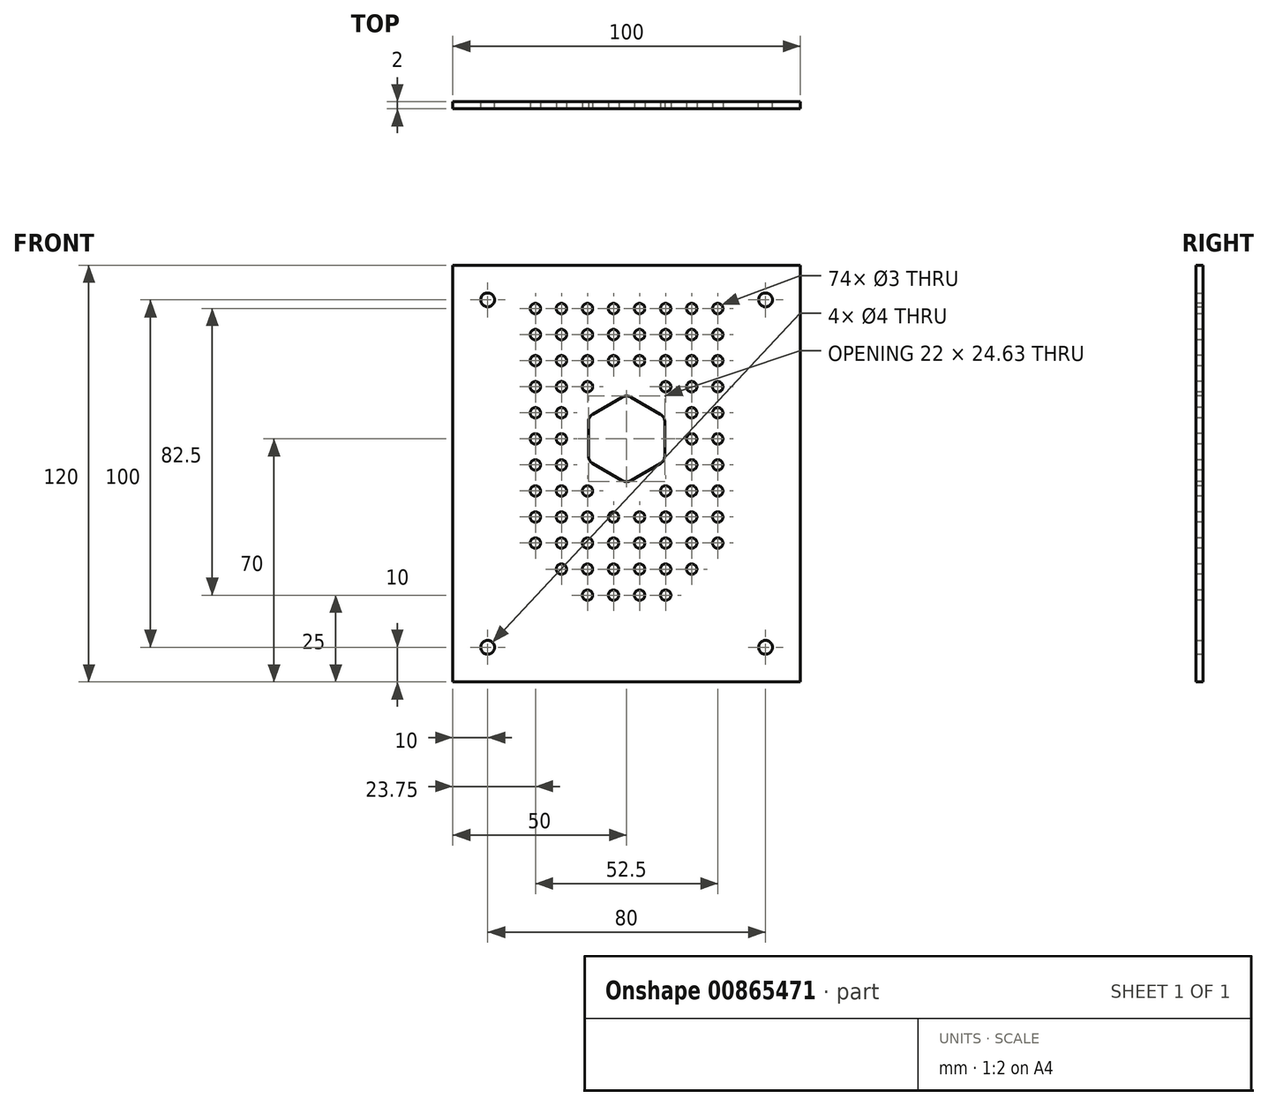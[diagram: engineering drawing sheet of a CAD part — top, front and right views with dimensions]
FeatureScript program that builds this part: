
annotation { "Feature Type Name" : "Feature", "Feature Type Description" : "" }
export const myFeature = defineFeature(function(context is Context, id is Id, definition is map)
    precondition{}
    {
        {
            var Q0;
            Q0=qCreatedBy(makeId("Front.planeOp"),FACE);
            var sketch = newSketch(context, id + "F0", { "sketchPlane" : qUnion([Q0])});
            skLineSegment(sketch, "E0.bottom", {"start": v(50, 60) * mm, "end": v(-50, 60) * mm});
            skLineSegment(sketch, "E0.top", {"start": v(50, -60) * mm, "end": v(-50, -60) * mm});
            skLineSegment(sketch, "E0.left", {"start": v(50, 60) * mm, "end": v(50, -60) * mm});
            skLineSegment(sketch, "E0.right", {"start": v(-50, 60) * mm, "end": v(-50, -60) * mm});
            skPoint(sketch, "E0.middle", {"position": v(0, 0) * mm});
            skCircle(sketch, "E1", {"center": v(-40, 50) * mm, "radius": 2 * mm});
            skCircle(sketch, "E2", {"center": v(40, 50) * mm, "radius": 2 * mm});
            skCircle(sketch, "E3", {"center": v(40, -50) * mm, "radius": 2 * mm});
            skCircle(sketch, "E4", {"center": v(-40, -50) * mm, "radius": 2 * mm});
            skSolve(sketch);
        }
        {
            var Q0;
            Q0 = qSketchRegion(id + "F0", true);
            extrude(context, id + "F1", {"entities" : qUnion([Q0]), "depth" : 2 * mm, "offsetDistance" : 25 * mm});
        }
        {
            var Q0;
            Q0=makeQuery(id+"F1.opExtrude","CAP_FACE",FACE,{"disambiguationData":[OSD([sQuery(id+"F0.wireOp",EDGE,"E0.bottom"),sQuery(id+"F0.wireOp",EDGE,"E0.top"),sQuery(id+"F0.wireOp",EDGE,"E0.left"),sQuery(id+"F0.wireOp",EDGE,"E0.right"),sQuery(id+"F0.wireOp",EDGE,"E1"),sQuery(id+"F0.wireOp",EDGE,"E2"),sQuery(id+"F0.wireOp",EDGE,"E3"),sQuery(id+"F0.wireOp",EDGE,"E4")])],"isStart":false});
            var sketch = newSketch(context, id + "F2", { "sketchPlane" : qUnion([Q0])});
            skCircle(sketch, "E5.cCircle", {"center": v(0, 10) * mm, "radius": 11 * mm, "construction": true});
            skLineSegment(sketch, "E5.0", {"start": v(-9.75, 17.07) * mm, "end": v(-1.25, 21.98) * mm});
            skLineSegment(sketch, "E5.1", {"start": v(1.25, 21.98) * mm, "end": v(9.75, 17.07) * mm});
            skLineSegment(sketch, "E5.2", {"start": v(11, 14.9) * mm, "end": v(11, 5.1) * mm});
            skLineSegment(sketch, "E5.3", {"start": v(9.75, 2.93) * mm, "end": v(1.25, -1.98) * mm});
            skLineSegment(sketch, "E5.4", {"start": v(-1.25, -1.98) * mm, "end": v(-9.75, 2.93) * mm});
            skLineSegment(sketch, "E5.5", {"start": v(-11, 5.1) * mm, "end": v(-11, 14.9) * mm});
            skPoint(sketch, "E5.0.midPoint", {"position": v(-5.5, 19.53) * mm});
            skPoint(sketch, "E6.visualSharp", {"position": v(0, -2.7) * mm});
            skArc(sketch, "E6.filletArc", {"start": v(-1.25, -1.98) * mm, "mid": v(0, -2.31) * mm, "end": v(1.25, -1.98) * mm});
            skPoint(sketch, "E7.visualSharp", {"position": v(-11, 3.65) * mm});
            skArc(sketch, "E7.filletArc", {"start": v(-11, 5.1) * mm, "mid": v(-10.67, 3.84) * mm, "end": v(-9.75, 2.93) * mm});
            skPoint(sketch, "E8.visualSharp", {"position": v(-11, 16.35) * mm});
            skArc(sketch, "E8.filletArc", {"start": v(-9.75, 17.07) * mm, "mid": v(-10.67, 16.16) * mm, "end": v(-11, 14.9) * mm});
            skPoint(sketch, "E9.visualSharp", {"position": v(0, 22.7) * mm});
            skArc(sketch, "E9.filletArc", {"start": v(1.25, 21.98) * mm, "mid": v(0, 22.31) * mm, "end": v(-1.25, 21.98) * mm});
            skPoint(sketch, "E10.visualSharp", {"position": v(11, 16.35) * mm});
            skArc(sketch, "E10.filletArc", {"start": v(11, 14.9) * mm, "mid": v(10.67, 16.16) * mm, "end": v(9.75, 17.07) * mm});
            skPoint(sketch, "E11.visualSharp", {"position": v(11, 3.65) * mm});
            skArc(sketch, "E11.filletArc", {"start": v(9.75, 2.93) * mm, "mid": v(10.67, 3.84) * mm, "end": v(11, 5.1) * mm});
            skLineSegment(sketch, "E12", {"start": v(0, 10.35) * mm, "end": v(22.67, 10.35) * mm});
            skLineSegment(sketch, "E13", {"start": v(0, 10) * mm, "end": v(0, 22.7) * mm});
            skSolve(sketch);
        }
        {
            var Q0;
            Q0 = qSketchRegion(id + "F2", true);
            extrude(context, id + "F3", {"entities" : qUnion([Q0]), "operationType" : NewBodyOperationType.REMOVE, "oppositeDirection" : true, "depth" : 25 * mm, "offsetDistance" : 25 * mm});
        }
        {
            var Q0;
            Q0=makeQuery(id+"F1.opExtrude","CAP_FACE",FACE,{"disambiguationData":[OSD([sQuery(id+"F0.wireOp",EDGE,"E0.bottom"),sQuery(id+"F0.wireOp",EDGE,"E0.top"),sQuery(id+"F0.wireOp",EDGE,"E0.left"),sQuery(id+"F0.wireOp",EDGE,"E0.right"),sQuery(id+"F0.wireOp",EDGE,"E1"),sQuery(id+"F0.wireOp",EDGE,"E2"),sQuery(id+"F0.wireOp",EDGE,"E3"),sQuery(id+"F0.wireOp",EDGE,"E4")])],"isStart":false});
            var sketch = newSketch(context, id + "F4", { "sketchPlane" : qUnion([Q0])});
            skCircle(sketch, "E14", {"center": v(3.75, 47.5) * mm, "radius": 1.5 * mm});
            skCircle(sketch, "E15.0.1.0", {"center": v(3.75, 40) * mm, "radius": 1.5 * mm});
            skCircle(sketch, "E15.0.2.0", {"center": v(3.75, 32.5) * mm, "radius": 1.5 * mm});
            skCircle(sketch, "E15.1.0.0", {"center": v(11.25, 47.5) * mm, "radius": 1.5 * mm});
            skCircle(sketch, "E15.1.1.0", {"center": v(11.25, 40) * mm, "radius": 1.5 * mm});
            skCircle(sketch, "E15.1.2.0", {"center": v(11.25, 32.5) * mm, "radius": 1.5 * mm});
            skCircle(sketch, "E15.1.3.0", {"center": v(11.25, 25) * mm, "radius": 1.5 * mm});
            skCircle(sketch, "E15.2.0.0", {"center": v(18.75, 47.5) * mm, "radius": 1.5 * mm});
            skCircle(sketch, "E15.2.1.0", {"center": v(18.75, 40) * mm, "radius": 1.5 * mm});
            skCircle(sketch, "E15.2.2.0", {"center": v(18.75, 32.5) * mm, "radius": 1.5 * mm});
            skCircle(sketch, "E15.2.3.0", {"center": v(18.75, 25) * mm, "radius": 1.5 * mm});
            skCircle(sketch, "E15.2.4.0", {"center": v(18.75, 17.5) * mm, "radius": 1.5 * mm});
            skCircle(sketch, "E15.2.5.0", {"center": v(18.75, 10) * mm, "radius": 1.5 * mm});
            skCircle(sketch, "E15.2.6.0", {"center": v(18.75, 2.5) * mm, "radius": 1.5 * mm});
            skCircle(sketch, "E15.3.0.0", {"center": v(26.25, 47.5) * mm, "radius": 1.5 * mm});
            skCircle(sketch, "E15.3.1.0", {"center": v(26.25, 40) * mm, "radius": 1.5 * mm});
            skCircle(sketch, "E15.3.2.0", {"center": v(26.25, 32.5) * mm, "radius": 1.5 * mm});
            skCircle(sketch, "E15.3.3.0", {"center": v(26.25, 25) * mm, "radius": 1.5 * mm});
            skCircle(sketch, "E15.3.4.0", {"center": v(26.25, 17.5) * mm, "radius": 1.5 * mm});
            skCircle(sketch, "E15.3.5.0", {"center": v(26.25, 10) * mm, "radius": 1.5 * mm});
            skCircle(sketch, "E15.3.6.0", {"center": v(26.25, 2.5) * mm, "radius": 1.5 * mm});
            skLineSegment(sketch, "E15.direction1", {"start": v(3.75, 47.5) * mm, "end": v(11.25, 47.5) * mm, "construction": true});
            skLineSegment(sketch, "E15.direction2", {"start": v(3.75, 47.5) * mm, "end": v(3.75, 40) * mm, "construction": true});
            skCircle(sketch, "E16.0.0.8", {"center": v(3.75, -12.5) * mm, "radius": 1.5 * mm});
            skCircle(sketch, "E16.0.0.9", {"center": v(3.75, -20) * mm, "radius": 1.5 * mm});
            skCircle(sketch, "E16.0.0.10", {"center": v(3.75, -27.5) * mm, "radius": 1.5 * mm});
            skCircle(sketch, "E16.0.0.11", {"center": v(3.75, -35) * mm, "radius": 1.5 * mm});
            skCircle(sketch, "E16.0.1.7", {"center": v(11.25, -5) * mm, "radius": 1.5 * mm});
            skCircle(sketch, "E16.0.1.8", {"center": v(11.25, -12.5) * mm, "radius": 1.5 * mm});
            skCircle(sketch, "E16.0.1.9", {"center": v(11.25, -20) * mm, "radius": 1.5 * mm});
            skCircle(sketch, "E16.0.1.10", {"center": v(11.25, -27.5) * mm, "radius": 1.5 * mm});
            skCircle(sketch, "E16.0.1.11", {"center": v(11.25, -35) * mm, "radius": 1.5 * mm});
            skCircle(sketch, "E16.0.2.7", {"center": v(18.75, -5) * mm, "radius": 1.5 * mm});
            skCircle(sketch, "E16.0.2.8", {"center": v(18.75, -12.5) * mm, "radius": 1.5 * mm});
            skCircle(sketch, "E16.0.2.9", {"center": v(18.75, -20) * mm, "radius": 1.5 * mm});
            skCircle(sketch, "E16.0.2.10", {"center": v(18.75, -27.5) * mm, "radius": 1.5 * mm});
            skCircle(sketch, "E16.0.3.7", {"center": v(26.25, -5) * mm, "radius": 1.5 * mm});
            skCircle(sketch, "E16.0.3.8", {"center": v(26.25, -12.5) * mm, "radius": 1.5 * mm});
            skCircle(sketch, "E16.0.3.9", {"center": v(26.25, -20) * mm, "radius": 1.5 * mm});
            skCircle(sketch, "E17.MirrorC", {"center": v(-3.75, 47.5) * mm, "radius": 1.5 * mm});
            skCircle(sketch, "E18.MirrorC", {"center": v(-3.75, 40) * mm, "radius": 1.5 * mm});
            skCircle(sketch, "E19.MirrorC", {"center": v(-3.75, -12.5) * mm, "radius": 1.5 * mm});
            skCircle(sketch, "E20.MirrorC", {"center": v(-3.75, -35) * mm, "radius": 1.5 * mm});
            skCircle(sketch, "E21.MirrorC", {"center": v(-26.25, 17.5) * mm, "radius": 1.5 * mm});
            skCircle(sketch, "E22.MirrorC", {"center": v(-26.25, -12.5) * mm, "radius": 1.5 * mm});
            skCircle(sketch, "E23.MirrorC", {"center": v(-26.25, -5) * mm, "radius": 1.5 * mm});
            skCircle(sketch, "E24.MirrorC", {"center": v(-26.25, 47.5) * mm, "radius": 1.5 * mm});
            skCircle(sketch, "E25.MirrorC", {"center": v(-26.25, 32.5) * mm, "radius": 1.5 * mm});
            skCircle(sketch, "E26.MirrorC", {"center": v(-26.25, 10) * mm, "radius": 1.5 * mm});
            skCircle(sketch, "E27.MirrorC", {"center": v(-26.25, 40) * mm, "radius": 1.5 * mm});
            skCircle(sketch, "E28.MirrorC", {"center": v(-3.75, -27.5) * mm, "radius": 1.5 * mm});
            skCircle(sketch, "E29.MirrorC", {"center": v(-11.25, 40) * mm, "radius": 1.5 * mm});
            skCircle(sketch, "E30.MirrorC", {"center": v(-26.25, 2.5) * mm, "radius": 1.5 * mm});
            skCircle(sketch, "E31.MirrorC", {"center": v(-11.25, -27.5) * mm, "radius": 1.5 * mm});
            skCircle(sketch, "E32.MirrorC", {"center": v(-11.25, 32.5) * mm, "radius": 1.5 * mm});
            skCircle(sketch, "E33.MirrorC", {"center": v(-11.25, 47.5) * mm, "radius": 1.5 * mm});
            skCircle(sketch, "E34.MirrorC", {"center": v(-18.75, 25) * mm, "radius": 1.5 * mm});
            skCircle(sketch, "E35.MirrorC", {"center": v(-18.75, 10) * mm, "radius": 1.5 * mm});
            skCircle(sketch, "E36.MirrorC", {"center": v(-11.25, -35) * mm, "radius": 1.5 * mm});
            skCircle(sketch, "E37.MirrorC", {"center": v(-11.25, -20) * mm, "radius": 1.5 * mm});
            skCircle(sketch, "E38.MirrorC", {"center": v(-18.75, 2.5) * mm, "radius": 1.5 * mm});
            skCircle(sketch, "E39.MirrorC", {"center": v(-18.75, -12.5) * mm, "radius": 1.5 * mm});
            skLineSegment(sketch, "E40.MirrorCS", {"start": v(-3.75, 47.5) * mm, "end": v(-11.25, 47.5) * mm, "construction": true});
            skCircle(sketch, "E41.MirrorC", {"center": v(-11.25, -5) * mm, "radius": 1.5 * mm});
            skCircle(sketch, "E42.MirrorC", {"center": v(-11.25, -12.5) * mm, "radius": 1.5 * mm});
            skCircle(sketch, "E43.MirrorC", {"center": v(-18.75, -20) * mm, "radius": 1.5 * mm});
            skCircle(sketch, "E44.MirrorC", {"center": v(-18.75, 32.5) * mm, "radius": 1.5 * mm});
            skCircle(sketch, "E45.MirrorC", {"center": v(-26.25, 25) * mm, "radius": 1.5 * mm});
            skCircle(sketch, "E46.MirrorC", {"center": v(-26.25, -20) * mm, "radius": 1.5 * mm});
            skCircle(sketch, "E47.MirrorC", {"center": v(-11.25, 25) * mm, "radius": 1.5 * mm});
            skCircle(sketch, "E48.MirrorC", {"center": v(-3.75, 32.5) * mm, "radius": 1.5 * mm});
            skCircle(sketch, "E49.MirrorC", {"center": v(-18.75, 47.5) * mm, "radius": 1.5 * mm});
            skLineSegment(sketch, "E50.MirrorCS", {"start": v(-3.75, 47.5) * mm, "end": v(-3.75, 40) * mm, "construction": true});
            skCircle(sketch, "E51.MirrorC", {"center": v(-18.75, -5) * mm, "radius": 1.5 * mm});
            skCircle(sketch, "E52.MirrorC", {"center": v(-18.75, 40) * mm, "radius": 1.5 * mm});
            skCircle(sketch, "E53.MirrorC", {"center": v(-18.75, -27.5) * mm, "radius": 1.5 * mm});
            skCircle(sketch, "E54.MirrorC", {"center": v(-18.75, 17.5) * mm, "radius": 1.5 * mm});
            skCircle(sketch, "E55.MirrorC", {"center": v(-3.75, -20) * mm, "radius": 1.5 * mm});
            skSolve(sketch);
        }
        {
            var Q0;
            Q0 = qSketchRegion(id + "F4", true);
            extrude(context, id + "F5", {"entities" : qUnion([Q0]), "operationType" : NewBodyOperationType.REMOVE, "endBound" : BoundingType.THROUGH_ALL, "oppositeDirection" : true, "depth" : 25 * mm, "offsetDistance" : 25 * mm});
        }
    });
